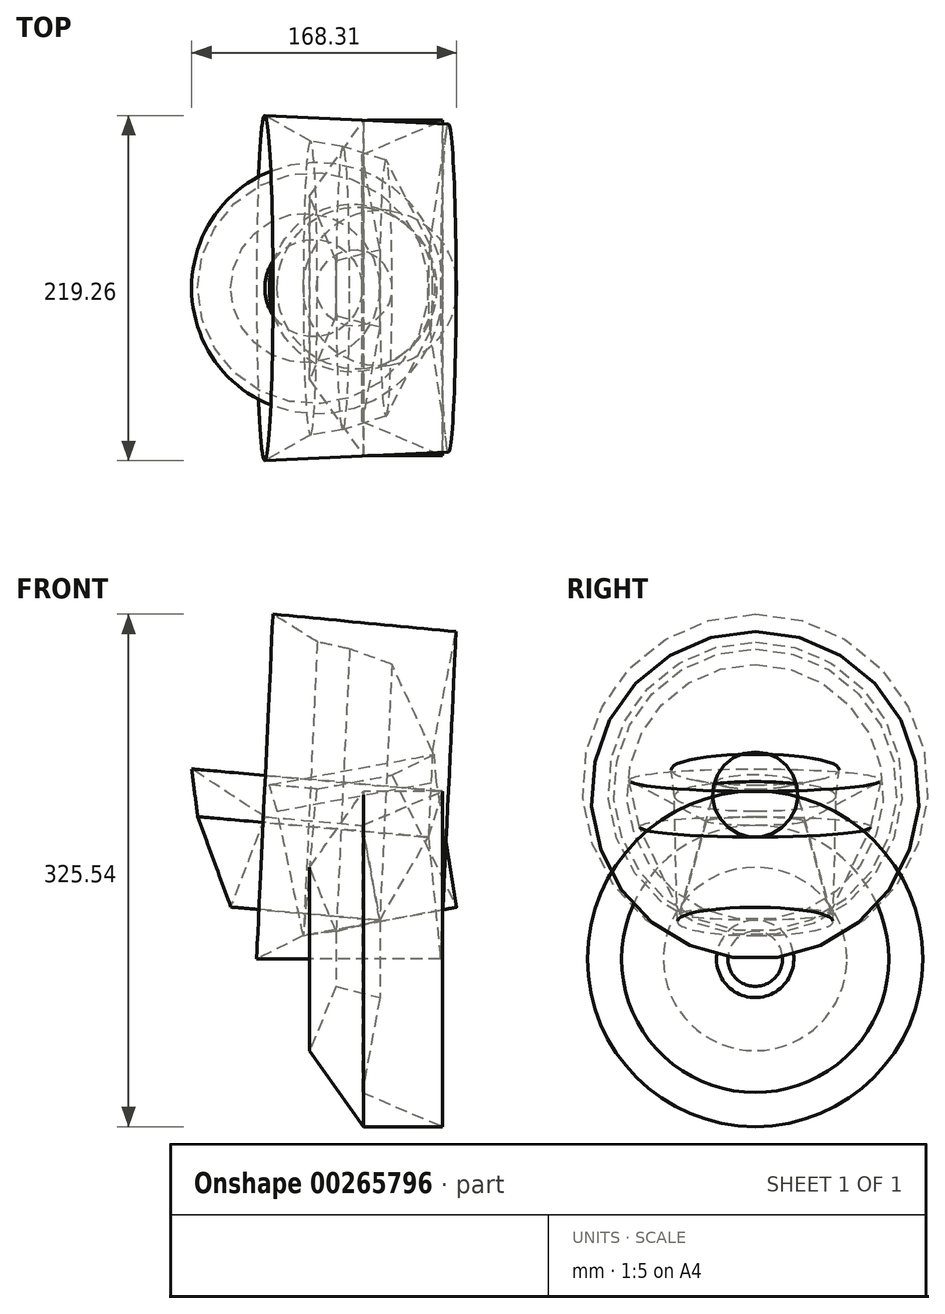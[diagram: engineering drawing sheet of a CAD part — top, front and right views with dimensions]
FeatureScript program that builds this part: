
annotation { "Feature Type Name" : "Feature", "Feature Type Description" : "" }
export const myFeature = defineFeature(function(context is Context, id is Id, definition is map)
    precondition{}
    {
        {
            var Q0;
            Q0=qCreatedBy(makeId("Front.planeOp"),FACE);
            var sketch = newSketch(context, id + "F0", { "sketchPlane" : qUnion([Q0])});
            skLineSegment(sketch, "E0", {"start": v(-47.12, 47.4) * mm, "end": v(-60.26, -46.55) * mm});
            skLineSegment(sketch, "E1", {"start": v(-60.26, -46.55) * mm, "end": v(56.54, -46.55) * mm});
            skLineSegment(sketch, "E2", {"start": v(56.54, -46.55) * mm, "end": v(48.83, 30.84) * mm});
            skLineSegment(sketch, "E3", {"start": v(48.83, 30.84) * mm, "end": v(18, -21.99) * mm});
            skLineSegment(sketch, "E4", {"start": v(18, -21.99) * mm, "end": v(6.85, 38.27) * mm});
            skLineSegment(sketch, "E5", {"start": v(6.85, 38.27) * mm, "end": v(57.97, 59.97) * mm});
            skLineSegment(sketch, "E6", {"start": v(57.97, 59.97) * mm, "end": v(7.71, 59.97) * mm});
            skLineSegment(sketch, "E7", {"start": v(7.71, 59.97) * mm, "end": v(-26.56, 11.7) * mm});
            skLineSegment(sketch, "E8", {"start": v(-26.56, 11.7) * mm, "end": v(-9.7, -29.13) * mm});
            skLineSegment(sketch, "E9", {"start": v(-9.7, -29.13) * mm, "end": v(-30.56, -31.7) * mm});
            skLineSegment(sketch, "E10", {"start": v(-30.56, -31.7) * mm, "end": v(-22.27, 61.4) * mm});
            skLineSegment(sketch, "E11", {"start": v(-22.27, 61.4) * mm, "end": v(-52.17, 64.06) * mm});
            skLineSegment(sketch, "E12", {"start": v(-52.17, 64.06) * mm, "end": v(-47.12, 47.4) * mm});
            skLineSegment(sketch, "E13", {"start": v(18, -21.99) * mm, "end": v(-9.7, -29.13) * mm});
            skLineSegment(sketch, "E14", {"start": v(-30.56, -31.7) * mm, "end": v(-60.26, -46.55) * mm});
            skLineSegment(sketch, "E15", {"start": v(-47.12, 47.4) * mm, "end": v(-30.56, -31.7) * mm});
            skLineSegment(sketch, "E16", {"start": v(-22.27, 61.4) * mm, "end": v(7.71, 59.97) * mm});
            skLineSegment(sketch, "E17", {"start": v(57.97, 59.97) * mm, "end": v(48.83, 30.84) * mm});
            skSolve(sketch);
        }
        {
            var Q0;
            Q0=makeQuery(id+"F0.imprint","IMPRINT",FACE,{"disambiguationData":[TD([[makeQuery(id+"F0.imprint","IMPRINT",EDGE,{"derivedFrom":sQuery(id+"F0.wireOp",EDGE,"E10")}),1.0]])]});
            var Q1;
            Q1=sQuery(id+"F0.wireOp",EDGE,"E4");
            revolve(context, id + "F1", {"entities" : qUnion([Q0]), "axis" : qUnion([Q1]), "revolveType" : RevolveType.FULL});
        }
        {
            var Q0;
            Q0=makeQuery(id+"F0.imprint","IMPRINT",FACE,{"disambiguationData":[TD([[makeQuery(id+"F0.imprint","IMPRINT",EDGE,{"derivedFrom":sQuery(id+"F0.wireOp",EDGE,"E4")}),1.0]])]});
            var Q1;
            Q1=sQuery(id+"F0.wireOp",EDGE,"E1");
            revolve(context, id + "F2", {"entities" : qUnion([Q0]), "axis" : qUnion([Q1]), "revolveType" : RevolveType.FULL});
        }
        {
            var Q0;
            Q0=makeQuery(id+"F0.imprint","IMPRINT",FACE,{"disambiguationData":[TD([[makeQuery(id+"F0.imprint","IMPRINT",EDGE,{"derivedFrom":sQuery(id+"F0.wireOp",EDGE,"E1")}),1.0]])]});
            var Q1;
            Q1=sQuery(id+"F0.wireOp",EDGE,"E16");
            revolve(context, id + "F3", {"entities" : qUnion([Q0]), "axis" : qUnion([Q1]), "revolveType" : RevolveType.FULL});
        }
        {
            var Q0;
            Q0=makeQuery(id+"F0.imprint","IMPRINT",FACE,{"disambiguationData":[TD([[makeQuery(id+"F0.imprint","IMPRINT",EDGE,{"derivedFrom":sQuery(id+"F0.wireOp",EDGE,"E3")}),-1.0]])]});
            var Q1;
            Q1=sQuery(id+"F0.wireOp",EDGE,"E10");
            revolve(context, id + "F4", {"entities" : qUnion([Q0]), "axis" : qUnion([Q1]), "revolveType" : RevolveType.FULL});
        }
    });
